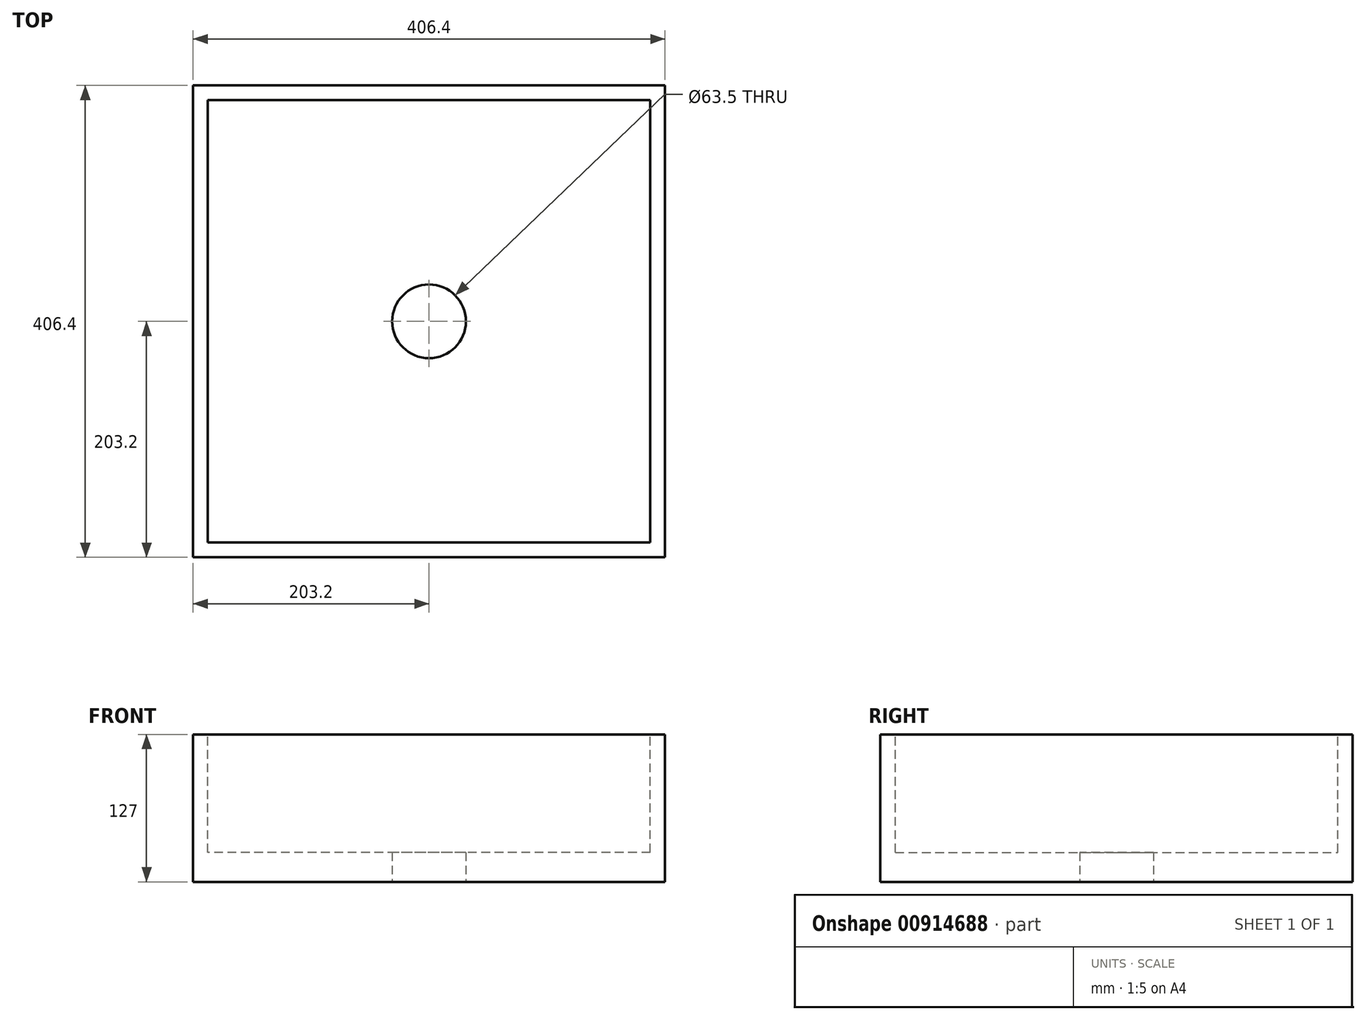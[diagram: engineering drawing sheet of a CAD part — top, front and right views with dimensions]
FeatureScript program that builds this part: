
annotation { "Feature Type Name" : "Feature", "Feature Type Description" : "" }
export const myFeature = defineFeature(function(context is Context, id is Id, definition is map)
    precondition{}
    {
        {
            var Q0;
            Q0=qCreatedBy(makeId("Top.planeOp"),FACE);
            var sketch = newSketch(context, id + "F0", { "sketchPlane" : qUnion([Q0])});
            skLineSegment(sketch, "E0.bottom", {"start": v(203.2, 203.2) * mm, "end": v(-203.2, 203.2) * mm});
            skLineSegment(sketch, "E0.top", {"start": v(203.2, -203.2) * mm, "end": v(-203.2, -203.2) * mm});
            skLineSegment(sketch, "E0.left", {"start": v(203.2, 203.2) * mm, "end": v(203.2, -203.2) * mm});
            skLineSegment(sketch, "E0.right", {"start": v(-203.2, 203.2) * mm, "end": v(-203.2, -203.2) * mm});
            skPoint(sketch, "E0.middle", {"position": v(0, 0) * mm});
            skCircle(sketch, "E1", {"center": v(0, 0) * mm, "radius": 31.75 * mm});
            skSolve(sketch);
        }
        {
            var Q0;
            Q0=makeQuery(id+"F0.imprint","IMPRINT",FACE,{"disambiguationData":[TD([[makeQuery(id+"F0.imprint","IMPRINT",EDGE,{"derivedFrom":sQuery(id+"F0.wireOp",EDGE,"E0.bottom")}),1.0]])]});
            extrude(context, id + "F1", {"entities" : qUnion([Q0]), "depth" : 127 * mm, "offsetDistance" : 25.4 * mm});
        }
        {
            var Q0;
            Q0=makeQuery(id+"F1.opExtrude","CAP_FACE",FACE,{"disambiguationData":[OSD([sQuery(id+"F0.wireOp",EDGE,"E0.bottom"),sQuery(id+"F0.wireOp",EDGE,"E0.top"),sQuery(id+"F0.wireOp",EDGE,"E0.left"),sQuery(id+"F0.wireOp",EDGE,"E0.right"),sQuery(id+"F0.wireOp",EDGE,"E1")])],"isStart":false});
            var sketch = newSketch(context, id + "F2", { "sketchPlane" : qUnion([Q0])});
            skLineSegment(sketch, "E2.bottom", {"start": v(190.5, -190.5) * mm, "end": v(-190.5, -190.5) * mm});
            skLineSegment(sketch, "E2.top", {"start": v(190.5, 190.5) * mm, "end": v(-190.5, 190.5) * mm});
            skLineSegment(sketch, "E2.left", {"start": v(190.5, -190.5) * mm, "end": v(190.5, 190.5) * mm});
            skLineSegment(sketch, "E2.right", {"start": v(-190.5, -190.5) * mm, "end": v(-190.5, 190.5) * mm});
            skPoint(sketch, "E2.middle", {"position": v(0, 0) * mm});
            skLineSegment(sketch, "E3.bottom", {"start": v(203.2, -203.2) * mm, "end": v(-203.2, -203.2) * mm});
            skLineSegment(sketch, "E3.top", {"start": v(203.2, 203.2) * mm, "end": v(-203.2, 203.2) * mm});
            skLineSegment(sketch, "E3.left", {"start": v(203.2, -203.2) * mm, "end": v(203.2, 203.2) * mm});
            skLineSegment(sketch, "E3.right", {"start": v(-203.2, -203.2) * mm, "end": v(-203.2, 203.2) * mm});
            skSolve(sketch);
        }
        {
            var Q0;
            Q0=makeQuery(id+"F2.imprint","IMPRINT",FACE,{"disambiguationData":[TD([[makeQuery(id+"F2.imprint","IMPRINT",EDGE,{"derivedFrom":sQuery(id+"F2.wireOp",EDGE,"E2.bottom")}),-1.0]])]});
            extrude(context, id + "F3", {"entities" : qUnion([Q0]), "operationType" : NewBodyOperationType.REMOVE, "oppositeDirection" : true, "depth" : 101.6 * mm, "offsetDistance" : 25.4 * mm});
        }
    });
